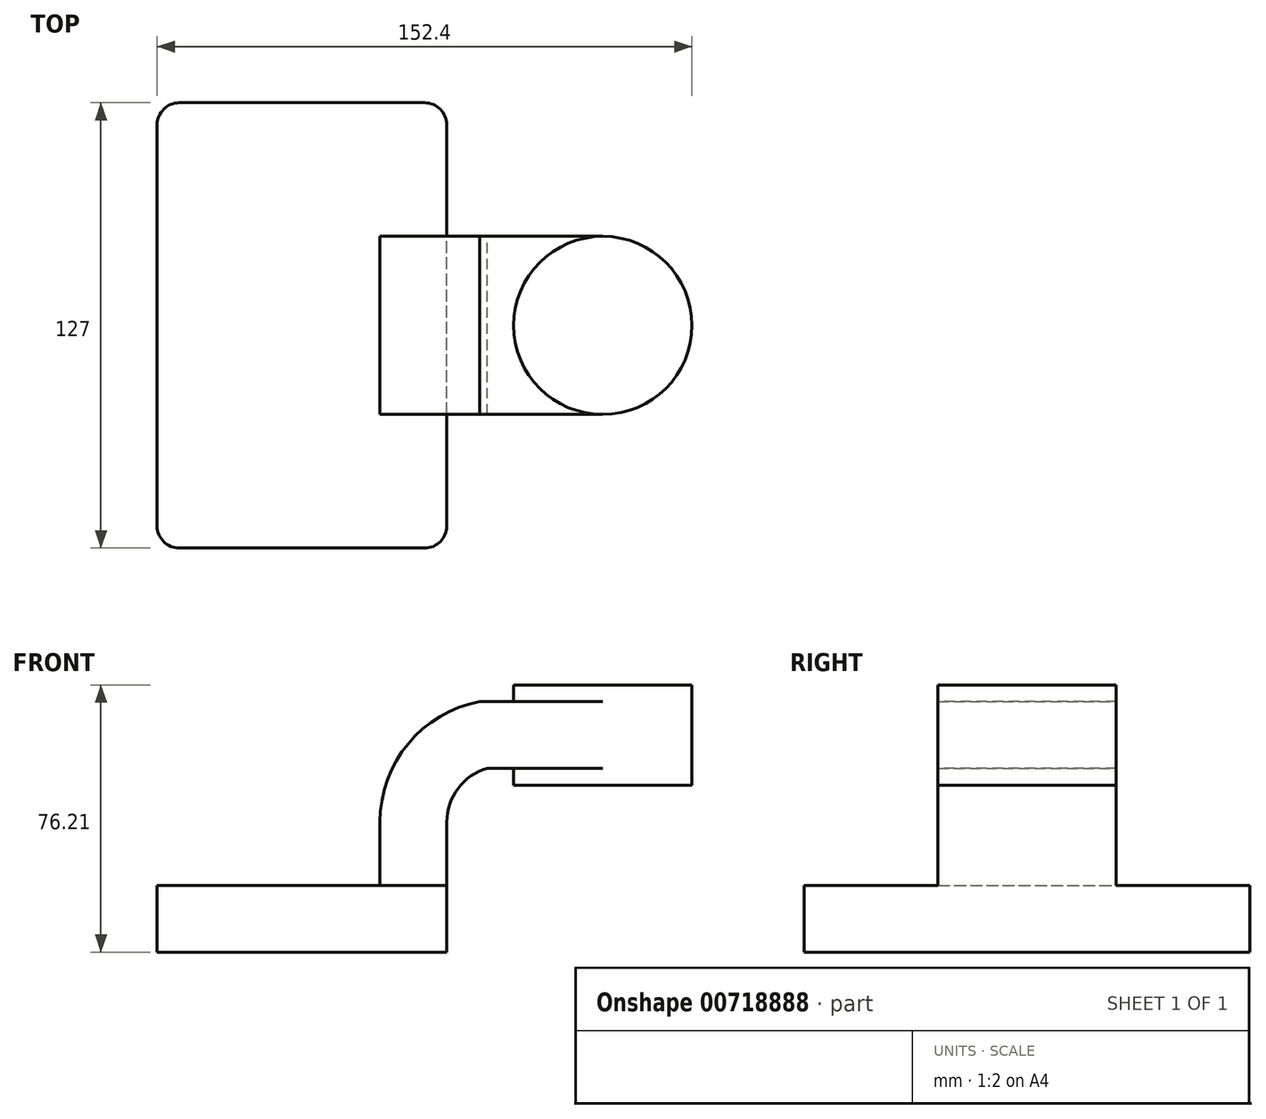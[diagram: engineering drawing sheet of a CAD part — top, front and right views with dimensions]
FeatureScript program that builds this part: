
annotation { "Feature Type Name" : "Feature", "Feature Type Description" : "" }
export const myFeature = defineFeature(function(context is Context, id is Id, definition is map)
    precondition{}
    {
        {
            var Q0;
            Q0=qCreatedBy(makeId("Front.planeOp"),FACE);
            var sketch = newSketch(context, id + "F0", { "sketchPlane" : qUnion([Q0])});
            skLineSegment(sketch, "E0.bottom", {"start": v(-41.28, 9.52) * mm, "end": v(41.27, 9.53) * mm});
            skLineSegment(sketch, "E0.top", {"start": v(-41.28, -9.53) * mm, "end": v(41.28, -9.53) * mm});
            skLineSegment(sketch, "E0.left", {"start": v(-41.28, 9.52) * mm, "end": v(-41.28, -9.53) * mm});
            skLineSegment(sketch, "E0.right", {"start": v(41.27, 9.53) * mm, "end": v(41.28, -9.52) * mm});
            skPoint(sketch, "E0.middle", {"position": v(0, 0) * mm});
            skLineSegment(sketch, "E1.bottom", {"start": v(60.32, 66.68) * mm, "end": v(111.12, 66.68) * mm});
            skLineSegment(sketch, "E1.top", {"start": v(60.32, 38.1) * mm, "end": v(111.12, 38.1) * mm});
            skLineSegment(sketch, "E1.left", {"start": v(60.32, 66.68) * mm, "end": v(60.32, 38.1) * mm});
            skLineSegment(sketch, "E1.right", {"start": v(111.12, 66.68) * mm, "end": v(111.12, 38.1) * mm});
            skPoint(sketch, "E1.middle", {"position": v(85.72, 52.39) * mm});
            skLineSegment(sketch, "E2", {"start": v(41.27, 9.53) * mm, "end": v(41.27, 27.6) * mm});
            skArc(sketch, "E3", {"start": v(41.28, 27.6) * mm, "mid": v(44.49, 37.17) * mm, "end": v(52.82, 42.88) * mm});
            skLineSegment(sketch, "E4", {"start": v(52.82, 42.88) * mm, "end": v(85.72, 42.88) * mm});
            skLineSegment(sketch, "E5.0", {"start": v(50.7, 61.93) * mm, "end": v(85.72, 61.93) * mm});
            skArc(sketch, "E5.1", {"start": v(22.23, 27.6) * mm, "mid": v(30.27, 49.9) * mm, "end": v(50.7, 61.93) * mm});
            skLineSegment(sketch, "E5.2", {"start": v(22.22, 9.53) * mm, "end": v(22.22, 27.6) * mm});
            skFitSpline(sketch, "E6", {"points": [v(-41.28, 9.52) * mm, v(50.7, 61.93) * mm], "startDerivative": vector(-0.98, 117.62) * mm, "endDerivative": vector(110.65, 4.74) * mm});
            skLineSegment(sketch, "E7", {"start": v(85.72, 66.68) * mm, "end": v(85.72, 38.1) * mm});
            skSolve(sketch);
        }
        {
            var Q0;
            Q0=makeQuery(id+"F0.imprint","IMPRINT",FACE,{"disambiguationData":[TD([[makeQuery(id+"F0.imprint","IMPRINT",EDGE,{"derivedFrom":sQuery(id+"F0.wireOp",EDGE,"E0.top")}),1.0]])]});
            extrude(context, id + "F1", {"entities" : qUnion([Q0]), "endBound" : BoundingType.SYMMETRIC, "depth" : 127 * mm, "offsetDistance" : 25.4 * mm});
        }
        {
            var Q0;
            {var subQ1=sQuery(id+"F0.wireOp",EDGE,"E2");Q0=makeQuery(id+"F0.imprint","IMPRINT",FACE,{"disambiguationData":[TD([[makeQuery(id+"F0.imprint","IMPRINT",EDGE,{"derivedFrom":subQ1}),1.0]])]});}
            extrude(context, id + "F2", {"entities" : qUnion([Q0]), "operationType" : NewBodyOperationType.ADD, "endBound" : BoundingType.SYMMETRIC, "depth" : 50.8 * mm, "offsetDistance" : 25.4 * mm});
        }
        {
            var Q0;
            Q0=makeQuery(id+"F0.imprint","IMPRINT",FACE,{"disambiguationData":[TD([[makeQuery(id+"F0.imprint","IMPRINT",EDGE,{"derivedFrom":sQuery(id+"F0.wireOp",EDGE,"E5.1")}),1.0]])]});
            extrude(context, id + "F3", {"entities" : qUnion([Q0]), "operationType" : NewBodyOperationType.ADD, "endBound" : BoundingType.SYMMETRIC, "depth" : 15.88 * mm, "offsetDistance" : 25.4 * mm});
        }
        {
            var Q0;
            Q0=makeQuery(id+"F1.opExtrude","CAP_EDGE",EDGE,{"disambiguationData":[OSD([sQuery(id+"F0.wireOp",EDGE,"E0.right")])],"isStart":false});
            var Q1;
            Q1=makeQuery(id+"F1.opExtrude","CAP_EDGE",EDGE,{"disambiguationData":[OSD([sQuery(id+"F0.wireOp",EDGE,"E0.left")])],"isStart":false});
            var Q2;
            Q2=makeQuery(id+"F1.opExtrude","CAP_EDGE",EDGE,{"disambiguationData":[OSD([sQuery(id+"F0.wireOp",EDGE,"E0.right")])],"isStart":true});
            var Q3;
            Q3=makeQuery(id+"F1.opExtrude","CAP_EDGE",EDGE,{"disambiguationData":[OSD([sQuery(id+"F0.wireOp",EDGE,"E0.left")])],"isStart":true});
            fillet(context, id + "F4", {"entities" : qUnion([Q0, Q1, Q2, Q3]), "radius" : 6.35 * mm, "tangentPropagation" : true, "allowEdgeOverflow" : false});
        }
        {
            var Q0;
            Q0=makeQuery(id+"F2.opExtrude","SWEPT_FACE",FACE,{"disambiguationData":[OSD([sQuery(id+"F0.wireOp",EDGE,"E1.left")])]});
            extrude(context, id + "F5", {"entities" : qUnion([Q0]), "operationType" : NewBodyOperationType.ADD, "depth" : 25.4 * mm, "offsetDistance" : 25.4 * mm});
        }
        {
            var Q0;
            {var subQ4=sQuery(id+"F0.wireOp",EDGE,"E1.right");Q0=makeQuery(id+"F0.imprint","IMPRINT",FACE,{"disambiguationData":[TD([[makeQuery(id+"F0.imprint","IMPRINT",EDGE,{"derivedFrom":subQ4}),-1.0]])]});}
            var Q1;
            Q1=sQuery(id+"F0.wireOp",EDGE,"E7");
            revolve(context, id + "F6", {"operationType" : NewBodyOperationType.ADD, "surfaceOperationType" : NewSurfaceOperationType.NEW, "entities" : qUnion([Q0]), "axis" : qUnion([Q1]), "revolveType" : RevolveType.FULL});
        }
    });
